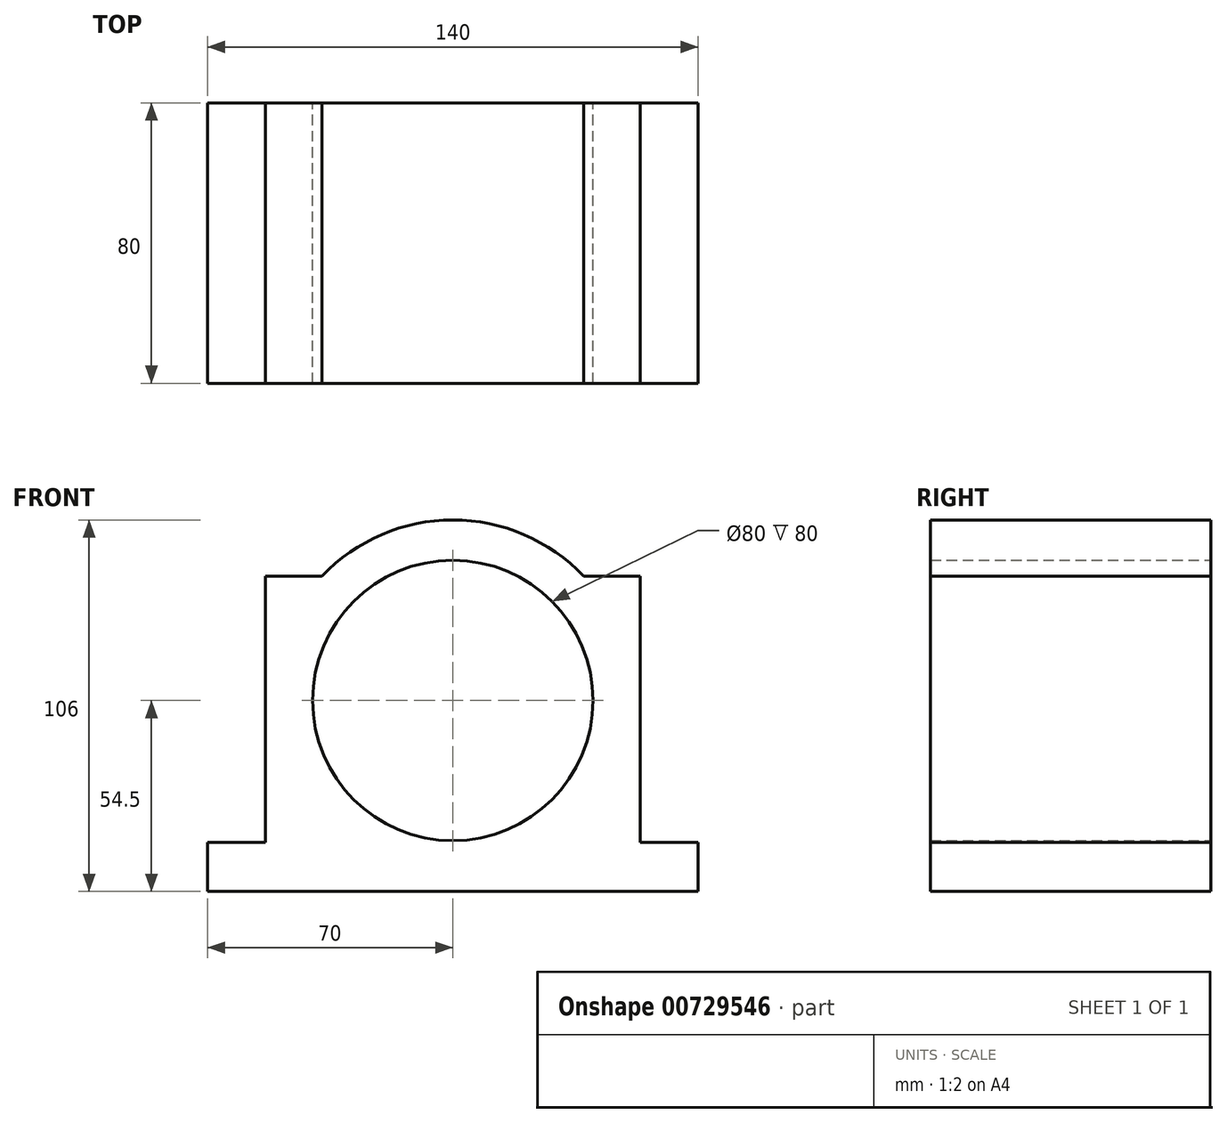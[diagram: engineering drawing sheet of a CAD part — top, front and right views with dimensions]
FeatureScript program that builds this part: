
annotation { "Feature Type Name" : "Feature", "Feature Type Description" : "" }
export const myFeature = defineFeature(function(context is Context, id is Id, definition is map)
    precondition{}
    {
        {
            var Q0;
            Q0=qCreatedBy(makeId("Front.planeOp"),FACE);
            var sketch = newSketch(context, id + "F0", { "sketchPlane" : qUnion([Q0])});
            skCircle(sketch, "E0", {"center": v(0, 0) * mm, "radius": 40 * mm});
            skArc(sketch, "E1", {"start": v(37.3, 35.5) * mm, "mid": v(0, 51.5) * mm, "end": v(-37.3, 35.5) * mm});
            skLineSegment(sketch, "E2", {"start": v(0, 77.44) * mm, "end": v(0, 51.5) * mm, "construction": true});
            skLineSegment(sketch, "E3.bottom", {"start": v(-70, -40.5) * mm, "end": v(-53.5, -40.5) * mm});
            skLineSegment(sketch, "E3.top", {"start": v(-70, -54.5) * mm, "end": v(70, -54.5) * mm});
            skLineSegment(sketch, "E3.left", {"start": v(-70, -40.5) * mm, "end": v(-70, -54.5) * mm});
            skLineSegment(sketch, "E3.right", {"start": v(70, -40.5) * mm, "end": v(70, -54.5) * mm});
            skPoint(sketch, "E3.middle", {"position": v(0, -47.5) * mm});
            skLineSegment(sketch, "E4.top", {"start": v(-53.5, 35.5) * mm, "end": v(-37.3, 35.5) * mm});
            skLineSegment(sketch, "E4.left", {"start": v(-53.5, -40.5) * mm, "end": v(-53.5, 35.5) * mm});
            skLineSegment(sketch, "E4.right", {"start": v(53.5, -40.5) * mm, "end": v(53.5, 35.5) * mm});
            skPoint(sketch, "E4.middle", {"position": v(0, -2.5) * mm});
            skLineSegment(sketch, "E5.trimOffspring", {"start": v(53.5, -40.5) * mm, "end": v(70, -40.5) * mm});
            skLineSegment(sketch, "E6", {"start": v(37.3, 35.5) * mm, "end": v(53.5, 35.5) * mm});
            skLineSegment(sketch, "E7", {"start": v(0, 51.5) * mm, "end": v(0, 40) * mm, "construction": true});
            skLineSegment(sketch, "E8", {"start": v(0, 40) * mm, "end": v(0, -54.5) * mm, "construction": true});
            skSolve(sketch);
        }
        {
            var Q0;
            Q0=makeQuery(id+"F0.imprint","IMPRINT",FACE,{"disambiguationData":[TD([[makeQuery(id+"F0.imprint","IMPRINT",EDGE,{"derivedFrom":sQuery(id+"F0.wireOp",EDGE,"E0")}),-1.0]])]});
            extrude(context, id + "F1", {"entities" : qUnion([Q0]), "depth" : 80 * mm, "offsetDistance" : 25 * mm, "symmetric" : true});
        }
    });
